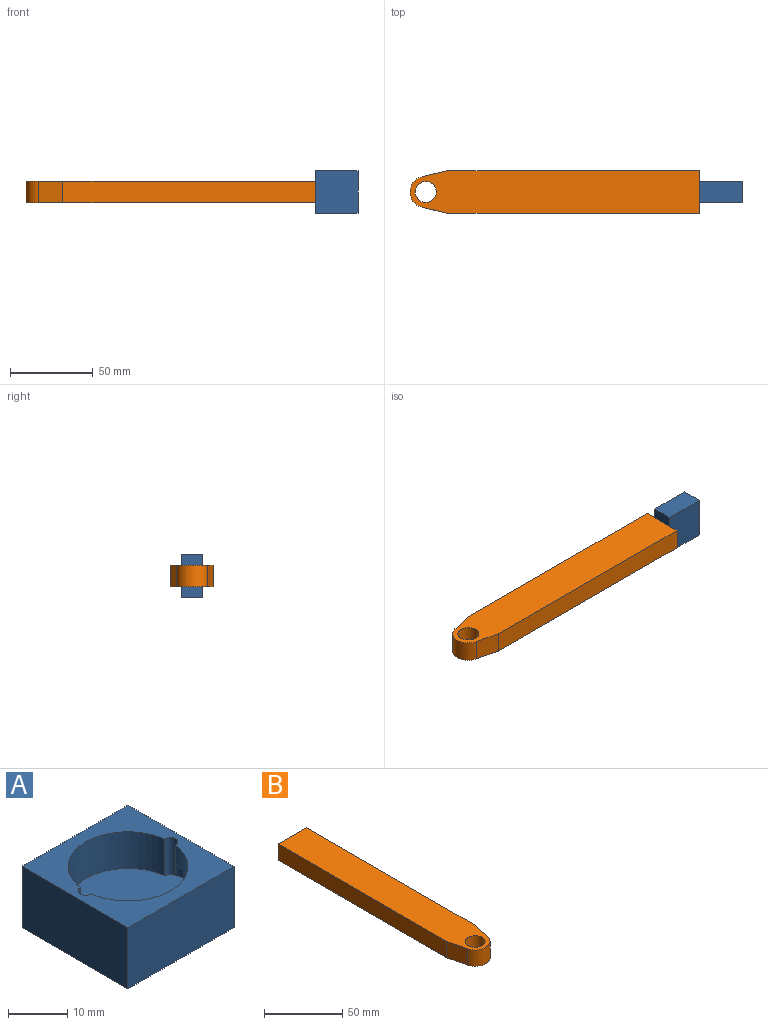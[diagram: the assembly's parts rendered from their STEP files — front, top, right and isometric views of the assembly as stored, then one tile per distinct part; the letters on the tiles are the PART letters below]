
ASSEMBLY  parts=2 mates=1
PART A: 16 faces, bbox 25.4x25.4x12.7 mm
  f0: cylinder r=10.16mm len=20.16mm, axis (0,0,1), area 212.7mm2, adj f1,f7,f9,f10,f11,f13,f14,f15
  f1: cylinder r=1.27mm len=7.62mm, axis (0,0,1), area 23.8mm2, adj f0,f2,f7,f10,f14,f15
  f2: cylinder r=10.16mm len=20.16mm, axis (0,0,1), area 215.7mm2, adj f1,f7,f9,f10,f12,f13
  f3: plane 25.4x12.7mm, normal (0,-1,0), area 322.6mm2, adj f4,f6,f7,f8
  f4: plane 25.4x12.7mm, normal (1,0,0), area 322.6mm2, adj f3,f5,f7,f8
  f5: plane 25.4x12.7mm, normal (0,1,0), area 322.6mm2, adj f4,f6,f7,f8
  f6: plane 25.4x12.7mm, normal (-1,0,0), area 322.6mm2, adj f3,f5,f7,f8
  f7: plane 25.4x25.4mm, normal (0,0,1), area 315.7mm2, adj f0,f1,f2,f3,f4,f5,f6,f9
  f8: plane 25.4x25.4mm, normal (0,0,-1), area 645.2mm2, adj f3,f4,f5,f6
  f9: cylinder r=1.27mm len=3.81mm, axis (0,0,1), area 15.8mm2, adj f0,f2,f7,f11,f12
  f10: plane 23.5x20.32mm, normal (0,0,1), area 337.1mm2, adj f0,f1,f2,f13,f15
  f11: plane 1.07x0.71mm, normal (0,0,-1), area 0.1mm2, adj f0,f9,f13
  f12: plane 4.2x2.16mm, normal (0,0,-1), area 3.4mm2, adj f2,f9,f13
  f13: cylinder r=2.54mm len=4.91mm, axis (0,0,-1), area 25.7mm2, adj f0,f2,f10,f11,f12
  f14: plane 3.77x2.33mm, normal (0,0,-1), area 4.2mm2, adj f0,f1,f15
  f15: cylinder r=2.54mm len=3.81mm, axis (0,0,-1), area 19.3mm2, adj f0,f1,f10,f14
PART B: 9 faces, bbox 25.4x174.6x12.7 mm
  f0: plane 25.4x12.7mm, normal (0,1,0), area 322.6mm2, adj f1,f5,f7,f8
  f1: plane 152.4x12.7mm, normal (-1,0,0), area 1935.5mm2, adj f0,f2,f7,f8
  f2: plane 14.84x12.7mm, normal (-0.97,-0.22,0), area 193.4mm2, adj f1,f3,f7,f8
  f3: cylinder r=9.53mm len=18.56mm, axis (0,0,-1), area 325.3mm2, adj f2,f4,f7,f8
  f4: plane 14.84x12.7mm, normal (0.97,-0.22,0), area 193.4mm2, adj f3,f5,f7,f8
  f5: plane 152.4x12.7mm, normal (1,0,0), area 1935.5mm2, adj f0,f4,f7,f8
  f6: cylinder r=6.35mm len=12.7mm, axis (0,0,-1), area 506.7mm2, adj f7,f8
  f7: plane 174.63x25.4mm, normal (0,0,1), area 4172.6mm2, adj f0,f1,f2,f3,f4,f5,f6
  f8: plane 174.63x25.4mm, normal (0,0,-1), area 4172.6mm2, adj f0,f1,f2,f3,f4,f5,f6
PLACE A rot(axis=(-1,0,0),90deg) t=(55.69,-135.01,79.84)mm
PLACE B rot(axis=(0,0,-1),90deg) t=(-33.25,-128.66,73.49)mm
MATE fastened A.f6 <-> B.f0  axis (-1,0,0) through (42.99,-128.66,79.84)mm
